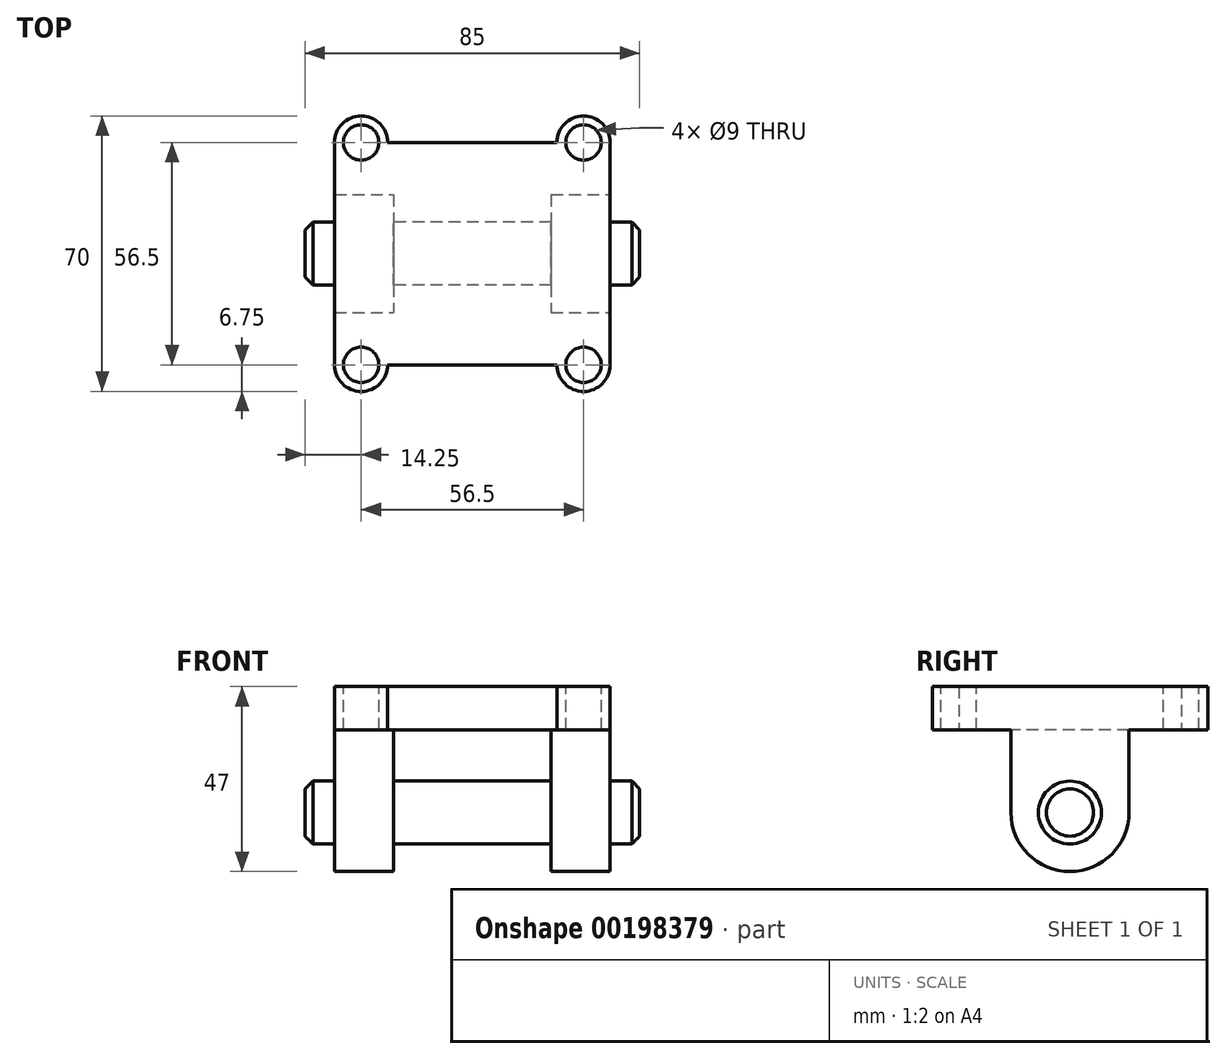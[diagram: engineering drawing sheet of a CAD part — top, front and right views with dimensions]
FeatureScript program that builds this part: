
annotation { "Feature Type Name" : "Feature", "Feature Type Description" : "" }
export const myFeature = defineFeature(function(context is Context, id is Id, definition is map)
    precondition{}
    {
        {
            var Q0;
            Q0=qCreatedBy(makeId("Top.planeOp"),FACE);
            var sketch = newSketch(context, id + "F0", { "sketchPlane" : qUnion([Q0])});
            skArc(sketch, "E0", {"start": v(-21.5, 28.25) * mm, "mid": v(-28.25, 35) * mm, "end": v(-35, 28.25) * mm});
            skLineSegment(sketch, "E1", {"start": v(-35, 28.25) * mm, "end": v(-35, -28.4) * mm});
            skArc(sketch, "E2", {"start": v(-35, -28.25) * mm, "mid": v(-28.25, -35) * mm, "end": v(-21.5, -28.25) * mm});
            skArc(sketch, "E3", {"start": v(35, 28.25) * mm, "mid": v(28.25, 35) * mm, "end": v(21.5, 28.25) * mm});
            skArc(sketch, "E4", {"start": v(21.5, -28.25) * mm, "mid": v(28.25, -35) * mm, "end": v(35, -28.25) * mm});
            skLineSegment(sketch, "E5", {"start": v(-21.5, 28.25) * mm, "end": v(21.5, 28.25) * mm});
            skLineSegment(sketch, "E6", {"start": v(35, 28.25) * mm, "end": v(35, -28.25) * mm});
            skLineSegment(sketch, "E7", {"start": v(-21.5, -28.25) * mm, "end": v(21.5, -28.25) * mm});
            skSolve(sketch);
        }
        {
            var Q0;
            Q0 = qSketchRegion(id + "F0", true);
            extrude(context, id + "F1", {"entities" : qUnion([Q0]), "depth" : 11 * mm});
        }
        {
            var Q0;
            Q0=makeQuery(id+"F1.opExtrude","CAP_FACE",FACE,{"disambiguationData":[OSD([sQuery(id+"F0.wireOp",EDGE,"E0"),sQuery(id+"F0.wireOp",EDGE,"E1"),sQuery(id+"F0.wireOp",EDGE,"E2"),sQuery(id+"F0.wireOp",EDGE,"E3"),sQuery(id+"F0.wireOp",EDGE,"E4"),sQuery(id+"F0.wireOp",EDGE,"E5"),sQuery(id+"F0.wireOp",EDGE,"E6"),sQuery(id+"F0.wireOp",EDGE,"E7")])],"isStart":false});
            var sketch = newSketch(context, id + "F2", { "sketchPlane" : qUnion([Q0])});
            skCircle(sketch, "E8", {"center": v(-28.25, 28.25) * mm, "radius": 4.5 * mm});
            skCircle(sketch, "E9", {"center": v(28.25, 28.25) * mm, "radius": 4.5 * mm});
            skCircle(sketch, "E10", {"center": v(28.25, -28.25) * mm, "radius": 4.5 * mm});
            skCircle(sketch, "E11", {"center": v(-28.25, -28.25) * mm, "radius": 4.5 * mm});
            skSolve(sketch);
        }
        {
            var Q0;
            Q0 = qSketchRegion(id + "F2", true);
            extrude(context, id + "F3", {"entities" : qUnion([Q0]), "operationType" : NewBodyOperationType.REMOVE, "endBound" : BoundingType.UP_TO_NEXT, "oppositeDirection" : true, "depth" : 25 * mm});
        }
        {
            var Q0;
            Q0=makeQuery(id+"F1.opExtrude","SWEPT_FACE",FACE,{"disambiguationData":[OSD([sQuery(id+"F0.wireOp",EDGE,"E6")])]});
            cPlane(context, id + "F4", {"entities" : qUnion([Q0]), "cplaneType" : CPlaneType.OFFSET, "offset" : 0 * mm, "width" : 150 * mm, "height" : 150 * mm});
        }
        {
            var Q0;
            Q0=qCreatedBy(id+"F4.planeOp",FACE);
            var sketch = newSketch(context, id + "F5", { "sketchPlane" : qUnion([Q0])});
            skLineSegment(sketch, "E12.0", {"start": v(15, 0) * mm, "end": v(-15, 0) * mm});
            skArc(sketch, "E13", {"start": v(-15, -21) * mm, "mid": v(0, -36) * mm, "end": v(15, -21) * mm});
            skLineSegment(sketch, "E14", {"start": v(0, 0) * mm, "end": v(0, -21) * mm, "construction": true});
            skLineSegment(sketch, "E15", {"start": v(15, -21) * mm, "end": v(15, 0) * mm});
            skLineSegment(sketch, "E16", {"start": v(-15, -21) * mm, "end": v(-15, 0) * mm});
            skCircle(sketch, "E17", {"center": v(0, -21) * mm, "radius": 8 * mm});
            skPoint(sketch, "E18.orphan", {"position": v(28.25, 0) * mm});
            skPoint(sketch, "E19.orphan", {"position": v(-28.25, 0) * mm});
            skSolve(sketch);
        }
        {
            var Q0;
            Q0 = qSketchRegion(id + "F5", true);
            var Q1;
            Q1=makeQuery(id+"F1.opExtrude","SWEPT_FACE",FACE,{"disambiguationData":[OSD([sQuery(id+"F0.wireOp",EDGE,"E1")])]});
            extrude(context, id + "F6", {"entities" : qUnion([Q0]), "operationType" : NewBodyOperationType.ADD, "endBound" : BoundingType.UP_TO_SURFACE, "oppositeDirection" : true, "endBoundEntityFace" : qUnion([Q1]), "depth" : 25 * mm});
        }
        {
            var Q0;
            {var subQ0=sQuery(id+"F0.wireOp",EDGE,"E4");var subQ1=sQuery(id+"F0.wireOp",EDGE,"E1");var subQ3=sQuery(id+"F0.wireOp",EDGE,"E2");var subQ4=sQuery(id+"F0.wireOp",EDGE,"E6");var subQ5=sQuery(id+"F0.wireOp",EDGE,"E7");Q0=makeQuery(id+"F6.boolean.opBoolean","SPLIT",FACE,{"disambiguationData":[TD([makeQuery(id+"F1.opExtrude","SWEPT_FACE",FACE,{"disambiguationData":[OSD([subQ3])]})])],"derivedFrom":makeQuery(id+"F1.opExtrude","CAP_FACE",FACE,{"disambiguationData":[OSD([sQuery(id+"F0.wireOp",EDGE,"E0"),subQ1,subQ3,sQuery(id+"F0.wireOp",EDGE,"E3"),subQ0,sQuery(id+"F0.wireOp",EDGE,"E5"),subQ4,subQ5])],"isStart":true})});}
            var sketch = newSketch(context, id + "F7", { "sketchPlane" : qUnion([Q0])});
            skLineSegment(sketch, "E20.bottom", {"start": v(20, -15) * mm, "end": v(-20, -15) * mm});
            skLineSegment(sketch, "E20.top", {"start": v(20, 15) * mm, "end": v(-20, 15) * mm});
            skLineSegment(sketch, "E20.left", {"start": v(20, -15) * mm, "end": v(20, 15) * mm});
            skLineSegment(sketch, "E20.right", {"start": v(-20, -15) * mm, "end": v(-20, 15) * mm});
            skSolve(sketch);
        }
        {
            var Q0;
            Q0 = qSketchRegion(id + "F7", true);
            extrude(context, id + "F8", {"entities" : qUnion([Q0]), "operationType" : NewBodyOperationType.REMOVE, "endBound" : BoundingType.THROUGH_ALL, "depth" : 25 * mm});
        }
        {
            var Q0;
            Q0=qCreatedBy(makeId("Right.planeOp"),FACE);
            var sketch = newSketch(context, id + "F9", { "sketchPlane" : qUnion([Q0])});
            skCircle(sketch, "E21.0", {"center": v(0, -21) * mm, "radius": 8 * mm});
            skSolve(sketch);
        }
        {
            var Q0;
            Q0 = qSketchRegion(id + "F9", true);
            extrude(context, id + "F10", {"entities" : qUnion([Q0]), "operationType" : NewBodyOperationType.ADD, "endBound" : BoundingType.SYMMETRIC, "depth" : 85 * mm});
        }
        {
            var Q0;
            Q0=makeQuery(id+"F10.opExtrude","CAP_EDGE",EDGE,{"disambiguationData":[OSD([sQuery(id+"F9.wireOp",EDGE,"E21.0")])],"isStart":false});
            var Q1;
            Q1=makeQuery(id+"F10.opExtrude","CAP_EDGE",EDGE,{"disambiguationData":[OSD([sQuery(id+"F9.wireOp",EDGE,"E21.0")])],"isStart":true});
            chamfer(context, id + "F11", {"entities" : qUnion([Q0, Q1]), "width" : 2 * mm, "tangentPropagation" : true});
        }
    });
